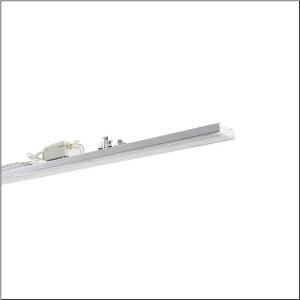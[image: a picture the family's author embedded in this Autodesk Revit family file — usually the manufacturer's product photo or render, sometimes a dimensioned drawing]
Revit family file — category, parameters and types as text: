
# Revit family: licross_11_recessed_ho_51tl12dv4m2md
name_source: partatom
category: Lighting Fixtures
units: mm (PartAtom-declared; Revit-internal decimal feet)

## family parameters
Cut with Voids When Loaded = No
Host = Face
Light Source = No
Part Type = Normal
Room Calculation Point = No
Round Connector Dimension = Use Diameter
Shared = No

## types (1)
- --- (1 x LED, 4070 lm, 21.7 W, 4000K)
    Apparent Load = 22 VA
    CIE Flux Codes = 66 91 98 100 100
    Color Rendering = 80
    Color Temperature = 4000K
    Default Elevation = 1800 mm
    Description = Licross 11 Recessed HO, luminaire insert, of sheet steel, coil coated, white, length: 2.250mm, width: 66mm, height: 67mm, LED rated luminous flux: 27.150lm, light colour: 840, SDCM (Standard Deviation of Colour Matching)MacAdam ≤ 2 SDCM (initial), control gear: DALI 2 (for two DALI lines), with plug, 6-pole, with phase selection, mains connection: 220..240V, AC/DC, 0/50..60Hz, rated input power: 151W, without changeover relay, for emergency light function, for central battery installations according to EN 60598-2-22, internal wiring halogen-free, primary optical cover: cover, of PMMA, light emission: direct distribution, primary light characteristic: symmetric, protection rating (complete): IP40, insulation class (complete): insulation class I (protective earthing), certification: CE, ENEC, VDE, UKCA, protection symbol: D if used in an environment without relevant dust loads with corresponding accessories, impact resistance: IK06, permissible ambient temperature for indoor applications: -40..+35°C, standard: EN 60598-2-22, corresponds to IFS (International Featured Standards) requirements for safety and quality in the food industry, reducing of maximum allowable ambient temperature of 5°C with ceiling mounting, LABS conformity tested according to VDMA 24364:2018-05, The light source and the operating device comply with the requirements of the Ecodesign Regulation (EU) 2019/2020 and are replaceable in accordance with this regulation, packaging unit: 1 piece
    Height = 58 mm
    Lamp = 1 x LED
    Lamp Light Flux = 4070 lm
    Lamp Power = 21.7 W
    Lamp count = 1
    Length = 2250 mm
    Luminous efficacy = 188 lm/W
    Manufacturer = Siteco
    ModVariant = No
    Model = 51TL12DV4M2MD
    Mounting Place = Ceiling
    Mounting Type = Pendant
    Number of Poles = 1
    OnlyDefault = Yes
    Power Factor = 1
    Product Name = Licross 11 Recessed HO
    Product group = luminaire insert | ceiling pendant
    ProductGroupID = 901
    Protection Class = Protection class I
    Protection Degree = IP 40
    RLX_Detail_Level = 1
    RLX_Emergency_Light_Flux = 0 lm
    RLX_Emergency_Type = 0
    RLX_Emergency_Type_DB = No
    RlxData = <blob elided: 29985 chars, md5=90ed6439>
    Socket = socket
    Standby Power = 0 W
    System Light Flux = 4070 lm
    System Power = 22 W
    Type Comments = : DC mode (central or group accumulator) initial emergency light level
    Type Image = l_1296930.jpg
    URL = http://relux.com
    VarID = @adj_092957
    Voltage = 0 V
    Weight = 0.00 kg
    Width = 66 mm

## geometry (parser evidence)
native form markers: Blend x4, Sweep x8
no freeform markers — native parametric forms only
